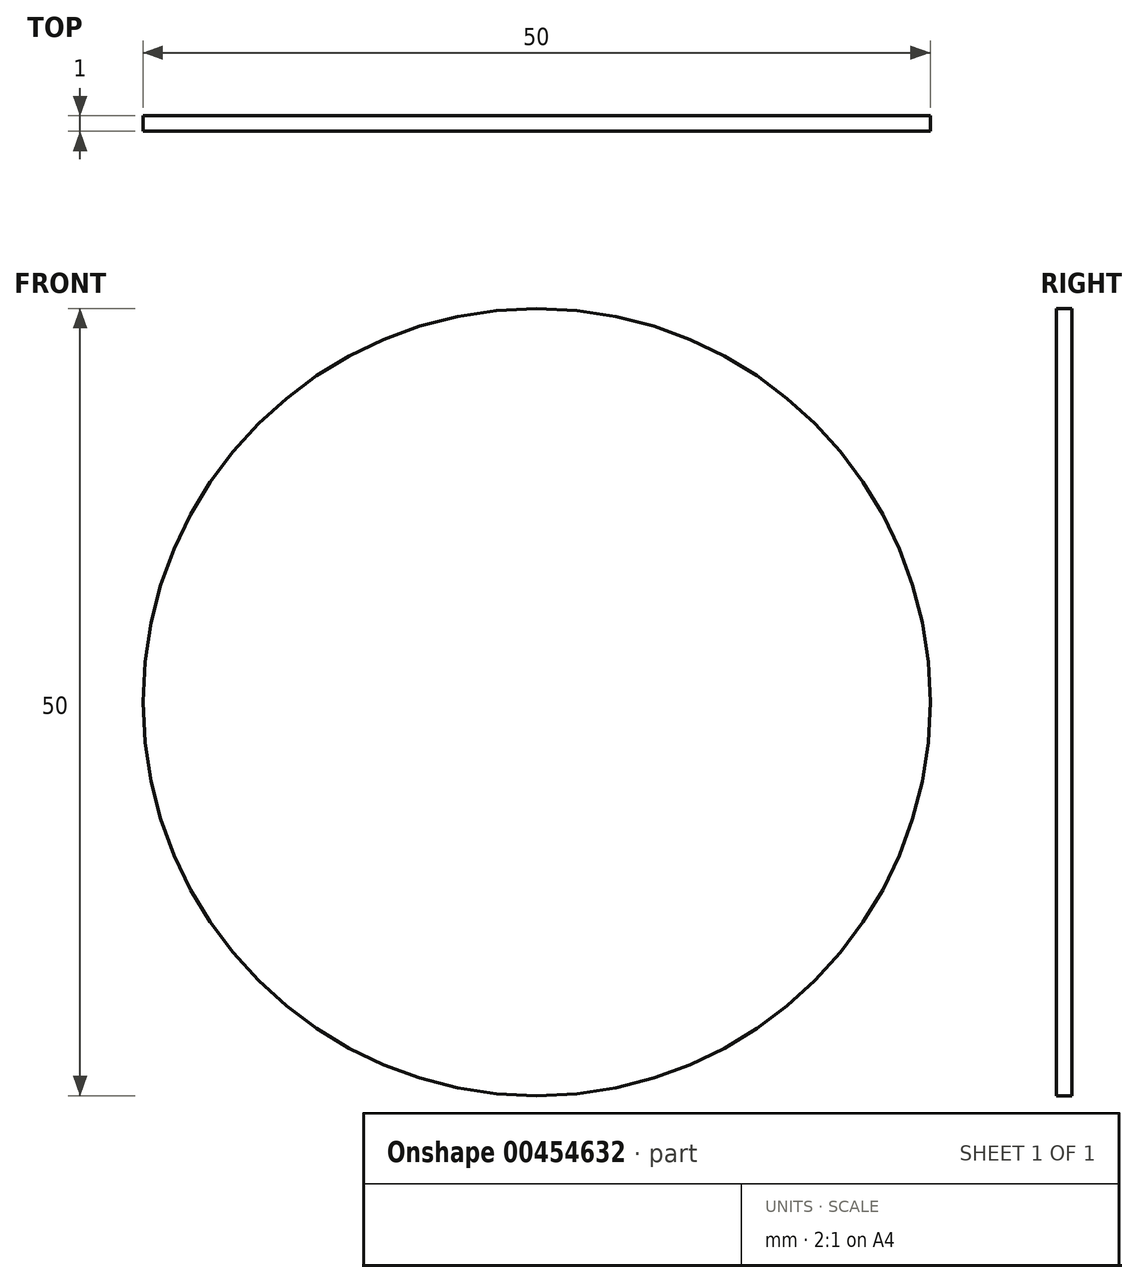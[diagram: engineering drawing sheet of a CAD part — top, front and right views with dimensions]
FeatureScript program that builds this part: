
annotation { "Feature Type Name" : "Feature", "Feature Type Description" : "" }
export const myFeature = defineFeature(function(context is Context, id is Id, definition is map)
    precondition{}
    {
        {
            var Q0;
            Q0=qCreatedBy(makeId("Front.planeOp"),FACE);
            var sketch = newSketch(context, id + "F0", { "sketchPlane" : qUnion([Q0])});
            skCircle(sketch, "E0", {"center": v(0, 0) * mm, "radius": 25 * mm});
            skSolve(sketch);
        }
        {
            var Q0;
            Q0=makeQuery(id+"F0.imprint","IMPRINT",FACE,{"disambiguationData":[TD([[makeQuery(id+"F0.imprint","IMPRINT",EDGE,{"derivedFrom":sQuery(id+"F0.wireOp",EDGE,"E0")}),1.0]])]});
            extrude(context, id + "F1", {"entities" : qUnion([Q0]), "depth" : 1 * mm});
        }
    });
